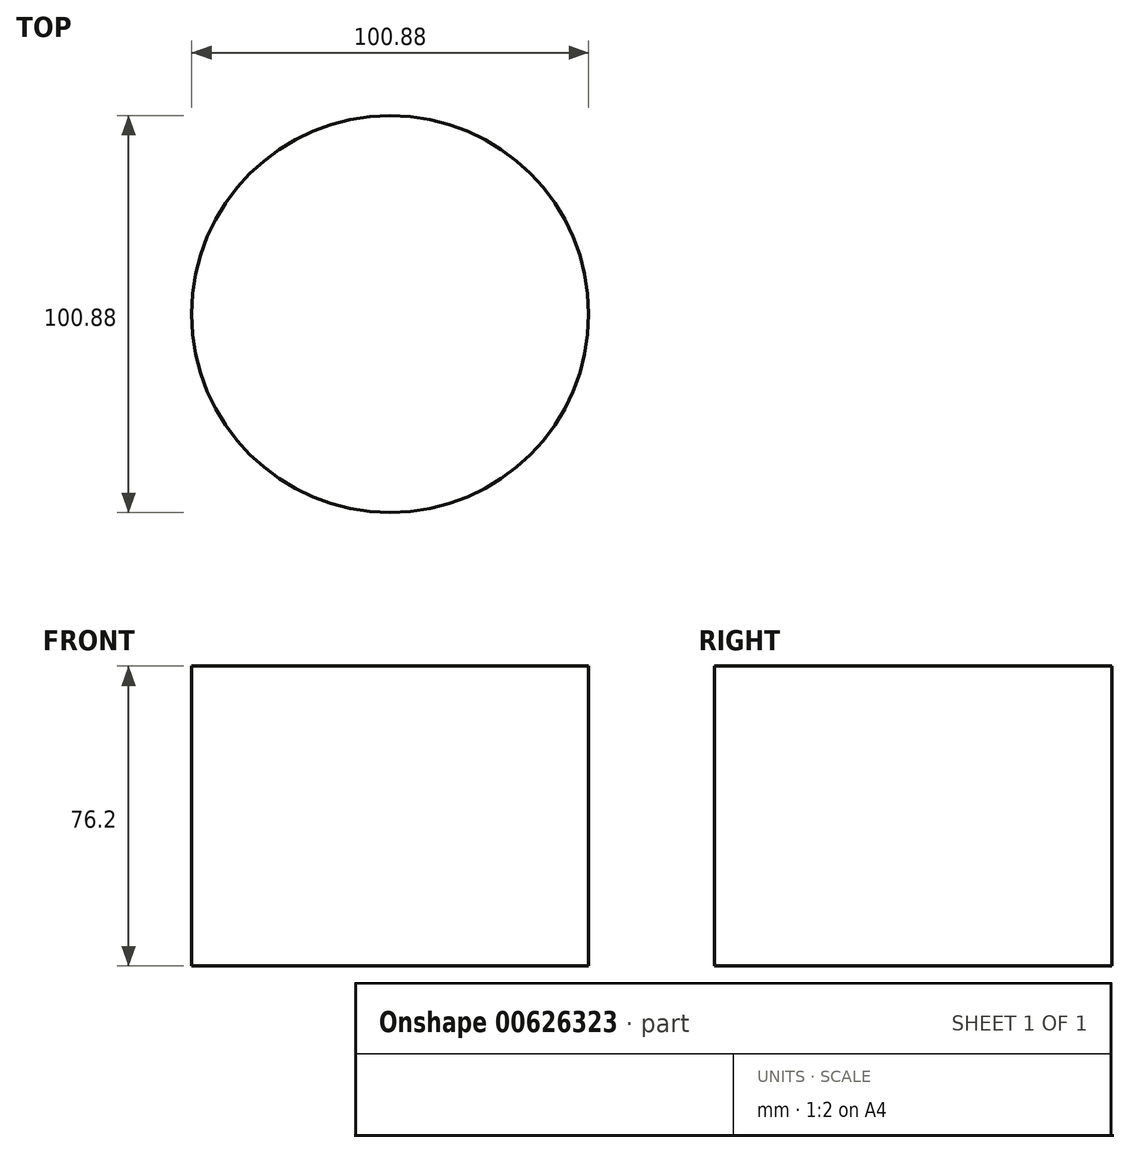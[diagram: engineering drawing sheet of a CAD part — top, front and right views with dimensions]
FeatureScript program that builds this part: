
annotation { "Feature Type Name" : "Feature", "Feature Type Description" : "" }
export const myFeature = defineFeature(function(context is Context, id is Id, definition is map)
    precondition{}
    {
        {
            var Q0;
            Q0=qCreatedBy(makeId("Top.planeOp"),FACE);
            var sketch = newSketch(context, id + "F0", { "sketchPlane" : qUnion([Q0])});
            skCircle(sketch, "E0", {"center": v(0, 0) * mm, "radius": 50.44 * mm});
            skSolve(sketch);
        }
        {
            var Q0;
            Q0=makeQuery(id+"F0.imprint","IMPRINT",FACE,{"disambiguationData":[TD([[makeQuery(id+"F0.imprint","IMPRINT",EDGE,{"derivedFrom":sQuery(id+"F0.wireOp",EDGE,"E0")}),1.0]])]});
            extrude(context, id + "F1", {"entities" : qUnion([Q0]), "depth" : 76.2 * mm, "offsetDistance" : 25.4 * mm});
        }
    });
